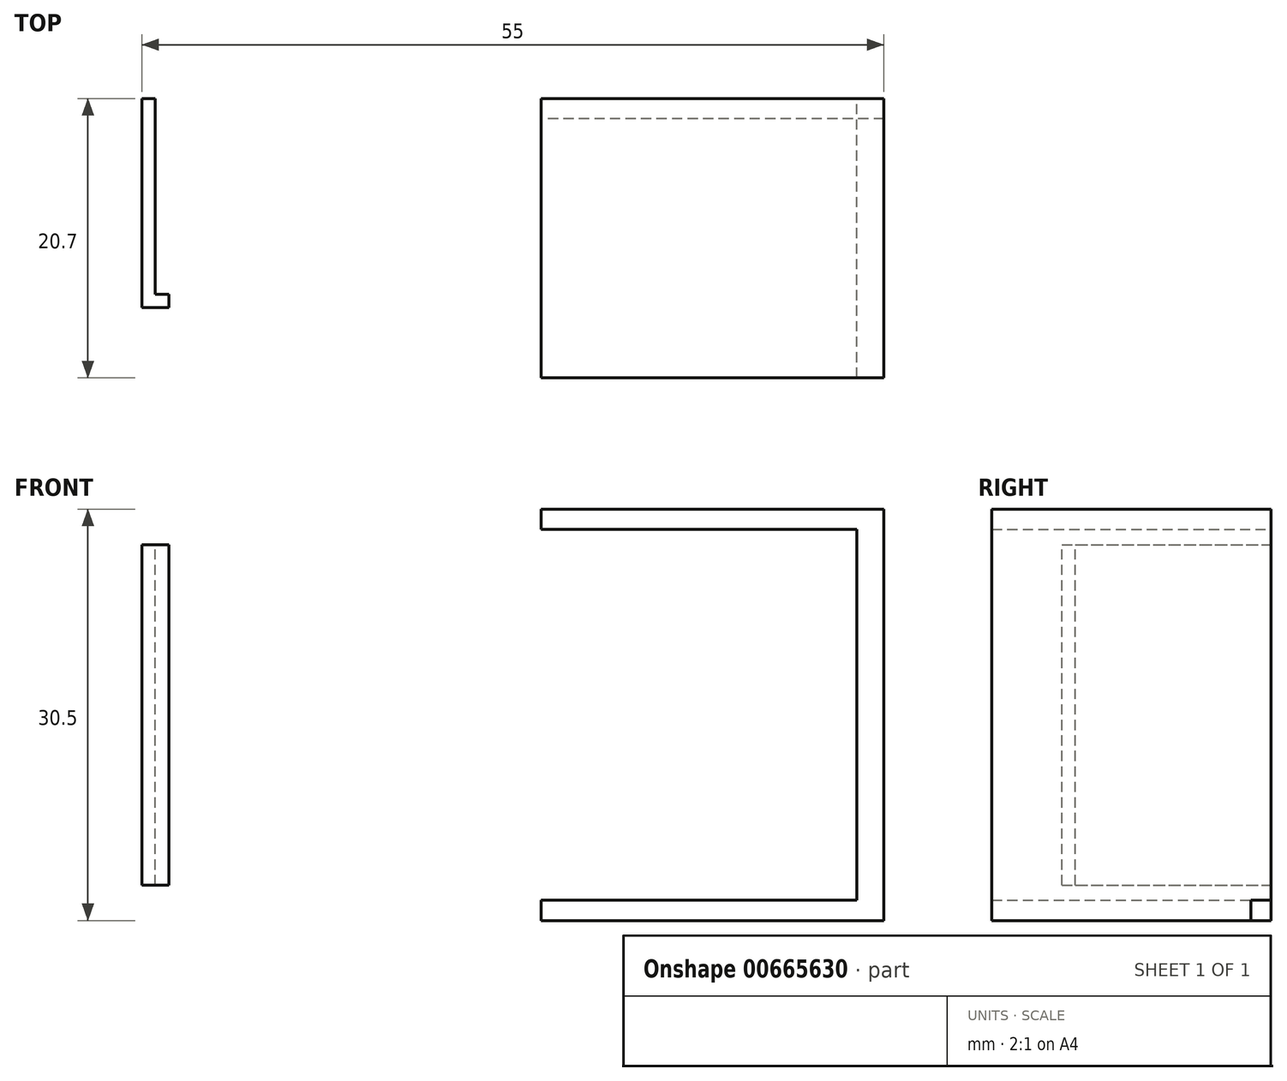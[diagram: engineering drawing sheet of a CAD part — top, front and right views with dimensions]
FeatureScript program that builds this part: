
annotation { "Feature Type Name" : "Feature", "Feature Type Description" : "" }
export const myFeature = defineFeature(function(context is Context, id is Id, definition is map)
    precondition{}
    {
        {
            var Q0;
            Q0=qCreatedBy(makeId("Front.planeOp"),FACE);
            var sketch = newSketch(context, id + "F0", { "sketchPlane" : qUnion([Q0])});
            skLineSegment(sketch, "E0.bottom", {"start": v(27.5, -15.25) * mm, "end": v(-27.5, -15.25) * mm});
            skLineSegment(sketch, "E0.top", {"start": v(27.5, 15.25) * mm, "end": v(-27.5, 15.25) * mm});
            skLineSegment(sketch, "E0.left", {"start": v(27.5, -15.25) * mm, "end": v(27.5, 15.25) * mm});
            skLineSegment(sketch, "E0.right", {"start": v(-27.5, -15.25) * mm, "end": v(-27.5, 15.25) * mm});
            skPoint(sketch, "E0.middle", {"position": v(0, 0) * mm});
            skLineSegment(sketch, "E1", {"start": v(2.1, -15.25) * mm, "end": v(2.1, -13.75) * mm});
            skLineSegment(sketch, "E2", {"start": v(2.1, -13.75) * mm, "end": v(27.5, -13.75) * mm});
            skLineSegment(sketch, "E3", {"start": v(27.5, -13.75) * mm, "end": v(27.5, -15.25) * mm});
            skLineSegment(sketch, "E4", {"start": v(2.1, -15.25) * mm, "end": v(27.5, -15.25) * mm});
            skLineSegment(sketch, "E5.MirrorCS", {"start": v(2.1, 13.75) * mm, "end": v(27.5, 13.75) * mm});
            skLineSegment(sketch, "E6.MirrorCS", {"start": v(2.1, 15.25) * mm, "end": v(2.1, 13.75) * mm});
            skLineSegment(sketch, "E7", {"start": v(25.5, -13.75) * mm, "end": v(25.5, 13.75) * mm});
            skLineSegment(sketch, "E8.bottom", {"start": v(-27.5, -12.62) * mm, "end": v(-26.5, -12.62) * mm});
            skLineSegment(sketch, "E8.top", {"start": v(-27.5, 12.62) * mm, "end": v(-26.5, 12.62) * mm});
            skLineSegment(sketch, "E8.left", {"start": v(-27.5, -12.62) * mm, "end": v(-27.5, 12.62) * mm});
            skLineSegment(sketch, "E8.right", {"start": v(-26.5, -12.62) * mm, "end": v(-26.5, 12.62) * mm});
            skPoint(sketch, "E8.middle", {"position": v(-27, 0) * mm});
            skSolve(sketch);
        }
        {
            var Q0;
            Q0=makeQuery(id+"F0.imprint","IMPRINT",FACE,{"disambiguationData":[TD([[makeQuery(id+"F0.imprint","IMPRINT",EDGE,{"derivedFrom":sQuery(id+"F0.wireOp",EDGE,"E8.bottom")}),1.0]])]});
            extrude(context, id + "F1", {"entities" : qUnion([Q0]), "depth" : 15.5 * mm, "offsetDistance" : 25.4 * mm});
        }
        {
            var Q0;
            {var subQ4=sQuery(id+"F0.wireOp",EDGE,"E6.MirrorCS");Q0=makeQuery(id+"F0.imprint","IMPRINT",FACE,{"disambiguationData":[TD([[makeQuery(id+"F0.imprint","IMPRINT",EDGE,{"derivedFrom":subQ4}),1.0]])]});}
            var Q1;
            {var subQ3=sQuery(id+"F0.wireOp",EDGE,"E1");Q1=makeQuery(id+"F0.imprint","IMPRINT",FACE,{"disambiguationData":[TD([[makeQuery(id+"F0.imprint","IMPRINT",EDGE,{"derivedFrom":subQ3}),-1.0]])]});}
            var Q2;
            {var subQ5=sQuery(id+"F0.wireOp",EDGE,"E7");Q2=makeQuery(id+"F0.imprint","IMPRINT",FACE,{"disambiguationData":[TD([[makeQuery(id+"F0.imprint","IMPRINT",EDGE,{"derivedFrom":subQ5}),-1.0]])]});}
            extrude(context, id + "F2", {"entities" : qUnion([Q0, Q1, Q2]), "depth" : 20.7 * mm, "offsetDistance" : 25.4 * mm});
        }
        {
            var Q0;
            {var subQ5=sQuery(id+"F0.wireOp",EDGE,"E0.bottom");Q0=makeQuery(id+"F0.imprint","IMPRINT",FACE,{"disambiguationData":[TD([[makeQuery(id+"F0.imprint","IMPRINT",EDGE,{"derivedFrom":subQ5}),-1.0]])]});}
            extrude(context, id + "F3", {"entities" : qUnion([Q0]), "depth" : 1.5 * mm, "offsetDistance" : 25.4 * mm});
        }
        {
            var Q0;
            Q0=makeQuery(id+"F1.opExtrude","SWEPT_FACE",FACE,{"disambiguationData":[OSD([sQuery(id+"F0.wireOp",EDGE,"E8.right")])]});
            var sketch = newSketch(context, id + "F4", { "sketchPlane" : qUnion([Q0])});
            skLineSegment(sketch, "E9.bottom", {"start": v(-15.5, -12.62) * mm, "end": v(-14.5, -12.62) * mm});
            skLineSegment(sketch, "E9.top", {"start": v(-15.5, 12.62) * mm, "end": v(-14.5, 12.62) * mm});
            skLineSegment(sketch, "E9.left", {"start": v(-15.5, -12.62) * mm, "end": v(-15.5, 12.62) * mm});
            skLineSegment(sketch, "E9.right", {"start": v(-14.5, -12.62) * mm, "end": v(-14.5, 12.62) * mm});
            skSolve(sketch);
        }
        {
            var Q0;
            Q0=makeQuery(id+"F4.imprint","IMPRINT",FACE,{"disambiguationData":[TD([[makeQuery(id+"F4.imprint","IMPRINT",EDGE,{"derivedFrom":sQuery(id+"F4.wireOp",EDGE,"E9.bottom")}),1.0]])]});
            extrude(context, id + "F5", {"entities" : qUnion([Q0]), "operationType" : NewBodyOperationType.ADD, "depth" : 1 * mm, "offsetDistance" : 25.4 * mm});
        }
    });
